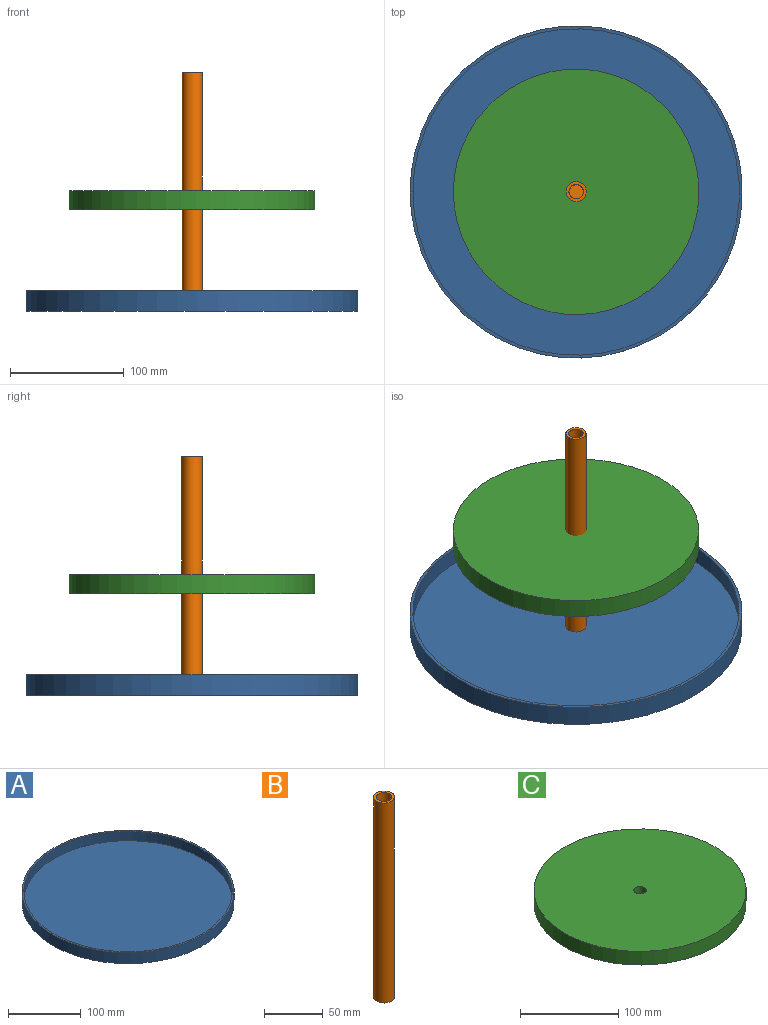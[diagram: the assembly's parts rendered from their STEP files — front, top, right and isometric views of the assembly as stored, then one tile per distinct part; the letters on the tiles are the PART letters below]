
ASSEMBLY  parts=3 mates=2
PART A: 5 faces, bbox 292.1x292.1x18.3 mm
  f0: cylinder r=146.05mm len=292.1mm, axis (0,0,-1), area 16782.2mm2, adj f1,f2
  f1: plane 292.1x292.1mm, normal (0,0,1), area 2310.6mm2, adj f0,f3
  f2: plane 292.1x292.1mm, normal (0,0,-1), area 67012.1mm2, adj f0
  f3: cylinder r=143.51mm len=287.02mm, axis (0,0,-1), area 14200mm2, adj f1,f4
  f4: plane 287.02x287.02mm, normal (0,0,1), area 64701.5mm2, adj f3
PART B: 5 faces, bbox 17.8x17.8x207.5 mm
  f0: cylinder r=8.89mm len=207.52mm, axis (0,0,-1), area 11591.4mm2, adj f1,f2
  f1: plane 17.78x17.78mm, normal (0,0,1), area 121.6mm2, adj f0,f3
  f2: plane 17.78x17.78mm, normal (0,0,-1), area 248.3mm2, adj f0
  f3: cylinder r=6.35mm len=204.98mm, axis (0,0,-1), area 8178.3mm2, adj f1,f4
  f4: plane 12.7x12.7mm, normal (0,0,1), area 126.7mm2, adj f3
PART C: 4 faces, bbox 215.9x215.9x17 mm
  f0: cylinder r=107.95mm len=215.9mm, axis (0,0,-1), area 11542.8mm2, adj f1,f2
  f1: plane 215.9x215.9mm, normal (0,0,1), area 36482.9mm2, adj f0,f3
  f2: plane 215.9x215.9mm, normal (0,0,-1), area 36482.9mm2, adj f0,f3
  f3: cylinder r=6.35mm len=17.02mm, axis (0,0,-1), area 679mm2, adj f1,f2
PLACE A rot(axis=(0,0,1),180deg) t=(-219.54,-111.91,27.66)mm
PLACE B t=(-219.23,-112.54,21.05)mm
PLACE C rot(axis=(0,0,1),180deg) t=(-219.23,-112.54,107.79)mm
MATE fastened A.f0 <-> B.f0  axis (0,0,1) through (-219.23,-112.54,21.05)mm
MATE revolute C.f0 <-> B.f0  axis (0,0,1) through (-219.23,-112.54,124.81)mm
